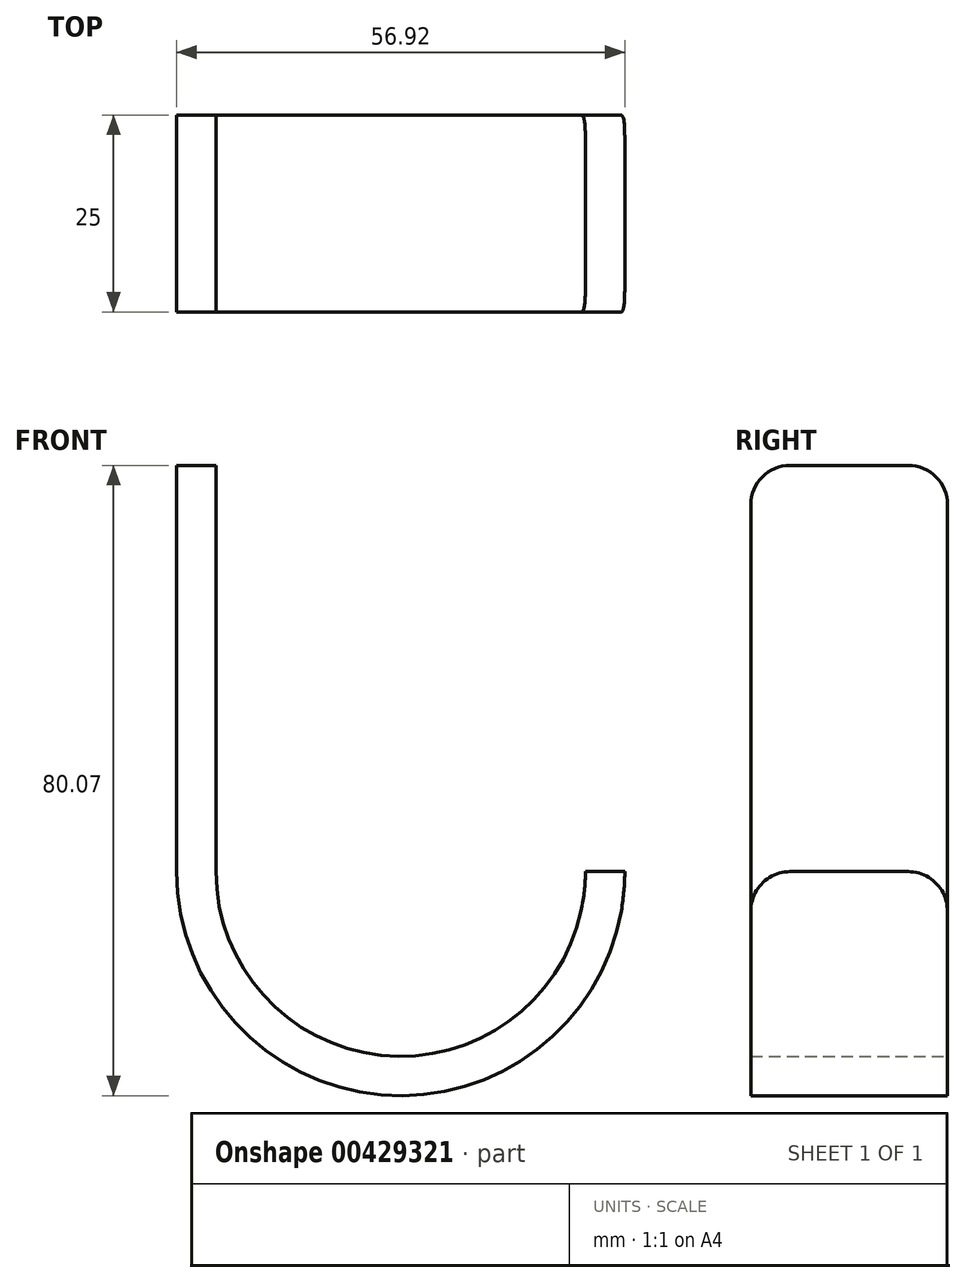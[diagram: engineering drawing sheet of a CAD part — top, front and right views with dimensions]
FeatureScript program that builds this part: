
annotation { "Feature Type Name" : "Feature", "Feature Type Description" : "" }
export const myFeature = defineFeature(function(context is Context, id is Id, definition is map)
    precondition{}
    {
        {
            var Q0;
            Q0=qCreatedBy(makeId("Front.planeOp"),FACE);
            var sketch = newSketch(context, id + "F0", { "sketchPlane" : qUnion([Q0])});
            skLineSegment(sketch, "E0", {"start": v(0, 0) * mm, "end": v(0, -51.6) * mm});
            skArc(sketch, "E1", {"start": v(0, -51.6) * mm, "mid": v(23.46, -75.07) * mm, "end": v(46.92, -51.6) * mm});
            skArc(sketch, "E2.0", {"start": v(-5, -51.6) * mm, "mid": v(23.46, -80.07) * mm, "end": v(51.92, -51.6) * mm});
            skLineSegment(sketch, "E2.1", {"start": v(-5, 0) * mm, "end": v(-5, -51.6) * mm});
            skLineSegment(sketch, "E3", {"start": v(-5, 0) * mm, "end": v(0, 0) * mm});
            skLineSegment(sketch, "E4", {"start": v(46.92, -51.6) * mm, "end": v(51.92, -51.6) * mm});
            skSolve(sketch);
        }
        {
            var Q0;
            Q0=makeQuery(id+"F0.imprint","IMPRINT",FACE,{"disambiguationData":[TD([[makeQuery(id+"F0.imprint","IMPRINT",EDGE,{"derivedFrom":sQuery(id+"F0.wireOp",EDGE,"E0")}),-1.0]])]});
            extrude(context, id + "F1", {"entities" : qUnion([Q0]), "depth" : 25 * mm});
        }
        {
            var Q0;
            Q0=makeQuery(id+"F1.opExtrude","CAP_EDGE",EDGE,{"disambiguationData":[OSD([sQuery(id+"F0.wireOp",EDGE,"E4")])],"isStart":false});
            var Q1;
            Q1=makeQuery(id+"F1.opExtrude","CAP_EDGE",EDGE,{"disambiguationData":[OSD([sQuery(id+"F0.wireOp",EDGE,"E4")])],"isStart":true});
            var Q2;
            Q2=makeQuery(id+"F1.opExtrude","CAP_EDGE",EDGE,{"disambiguationData":[OSD([sQuery(id+"F0.wireOp",EDGE,"E3")])],"isStart":true});
            var Q3;
            Q3=makeQuery(id+"F1.opExtrude","CAP_EDGE",EDGE,{"disambiguationData":[OSD([sQuery(id+"F0.wireOp",EDGE,"E3")])],"isStart":false});
            fillet(context, id + "F2", {"entities" : qUnion([Q0, Q1, Q2, Q3]), "radius" : 5 * mm, "tangentPropagation" : true, "allowEdgeOverflow" : false});
        }
    });
